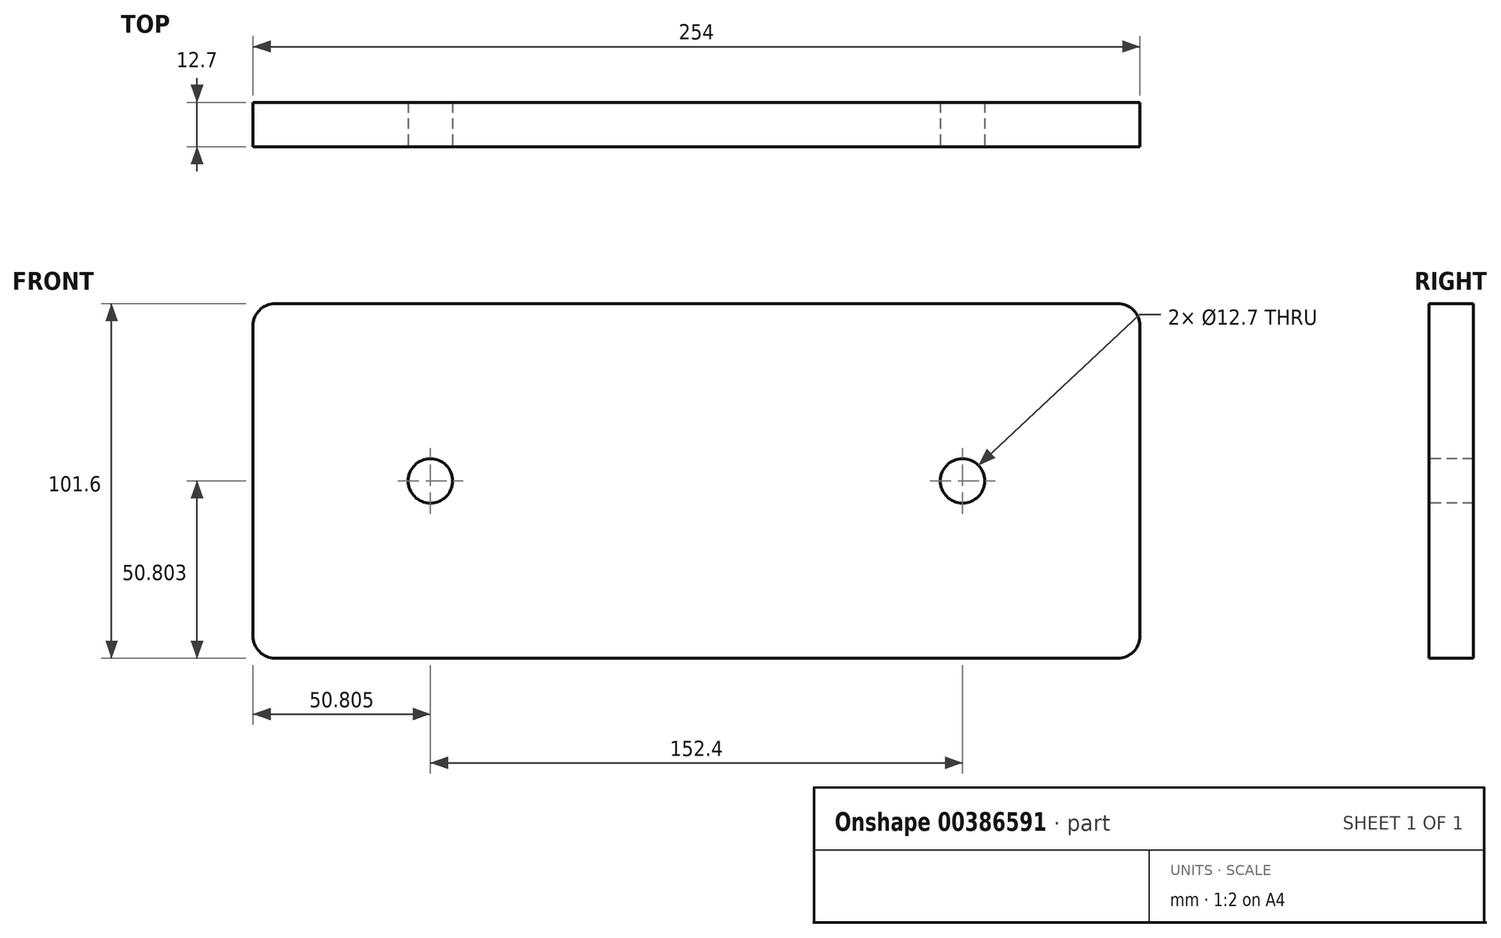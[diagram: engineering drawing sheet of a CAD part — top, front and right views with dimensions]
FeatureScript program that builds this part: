
annotation { "Feature Type Name" : "Feature", "Feature Type Description" : "" }
export const myFeature = defineFeature(function(context is Context, id is Id, definition is map)
    precondition{}
    {
        {
            var Q0;
            Q0=qCreatedBy(makeId("Front.planeOp"),FACE);
            var sketch = newSketch(context, id + "F0", { "sketchPlane" : qUnion([Q0])});
            skLineSegment(sketch, "E0.bottom", {"start": v(-225.2, -33.59) * mm, "end": v(28.8, -33.59) * mm});
            skLineSegment(sketch, "E0.top", {"start": v(-225.2, 68.01) * mm, "end": v(28.8, 68.01) * mm});
            skLineSegment(sketch, "E0.left", {"start": v(-225.2, -33.59) * mm, "end": v(-225.2, 68.01) * mm});
            skLineSegment(sketch, "E0.right", {"start": v(28.8, -33.59) * mm, "end": v(28.8, 68.01) * mm});
            skSolve(sketch);
        }
        {
            var Q0;
            Q0 = qSketchRegion(id + "F0", true);
            extrude(context, id + "F1", {"entities" : qUnion([Q0]), "depth" : 12.7 * mm});
        }
        {
            var Q0;
            Q0=makeQuery(id+"F1.opExtrude","CAP_FACE",FACE,{"disambiguationData":[OSD([sQuery(id+"F0.wireOp",EDGE,"E0.bottom"),sQuery(id+"F0.wireOp",EDGE,"E0.top"),sQuery(id+"F0.wireOp",EDGE,"E0.left"),sQuery(id+"F0.wireOp",EDGE,"E0.right")])],"isStart":false});
            var sketch = newSketch(context, id + "F2", { "sketchPlane" : qUnion([Q0])});
            skPoint(sketch, "E1", {"position": v(-174.4, 17.21) * mm});
            skPoint(sketch, "E2", {"position": v(-22, 17.21) * mm});
            skSolve(sketch);
        }
        {
            var Q0;
            Q0=makeQuery(id+"F1.opExtrude","SWEPT_EDGE",EDGE,{"disambiguationData":[OSD([sQuery(id+"F0.wireOp",EDGE,"E0.top"),sQuery(id+"F0.wireOp",EDGE,"E0.left")])]});
            var Q1;
            Q1=makeQuery(id+"F1.opExtrude","SWEPT_EDGE",EDGE,{"disambiguationData":[OSD([sQuery(id+"F0.wireOp",EDGE,"E0.top"),sQuery(id+"F0.wireOp",EDGE,"E0.right")])]});
            var Q2;
            Q2=makeQuery(id+"F1.opExtrude","SWEPT_EDGE",EDGE,{"disambiguationData":[OSD([sQuery(id+"F0.wireOp",EDGE,"E0.bottom"),sQuery(id+"F0.wireOp",EDGE,"E0.right")])]});
            var Q3;
            Q3=makeQuery(id+"F1.opExtrude","SWEPT_EDGE",EDGE,{"disambiguationData":[OSD([sQuery(id+"F0.wireOp",EDGE,"E0.bottom"),sQuery(id+"F0.wireOp",EDGE,"E0.left")])]});
            fillet(context, id + "F3", {"entities" : qUnion([Q0, Q1, Q2, Q3]), "radius" : 6.35 * mm, "tangentPropagation" : true, "allowEdgeOverflow" : false});
        }
        {
            var Q0;
            Q0=sQuery(id+"F2.wireOp",VERTEX,"E1");
            var Q1;
            Q1=sQuery(id+"F2.wireOp",VERTEX,"E2");
            var Q2;
            Q2=makeQuery(id+"F1.opExtrude","SWEPT_BODY",BODY,{"disambiguationData":[OSD([sQuery(id+"F0.wireOp",EDGE,"E0.bottom"),sQuery(id+"F0.wireOp",EDGE,"E0.top"),sQuery(id+"F0.wireOp",EDGE,"E0.left"),sQuery(id+"F0.wireOp",EDGE,"E0.right")])]});
            hole(context, id + "F4", {"style" : HoleStyle.SIMPLE, "endStyle" : HoleEndStyle.THROUGH, "holeDiameter" : 12.7 * mm, "isTappedThrough" : true, "tappedDepth" : 12.7 * mm, "tapClearance" : 3, "locations" : qUnion([Q0, Q1]), "scope" : qUnion([Q2])});
        }
    });
